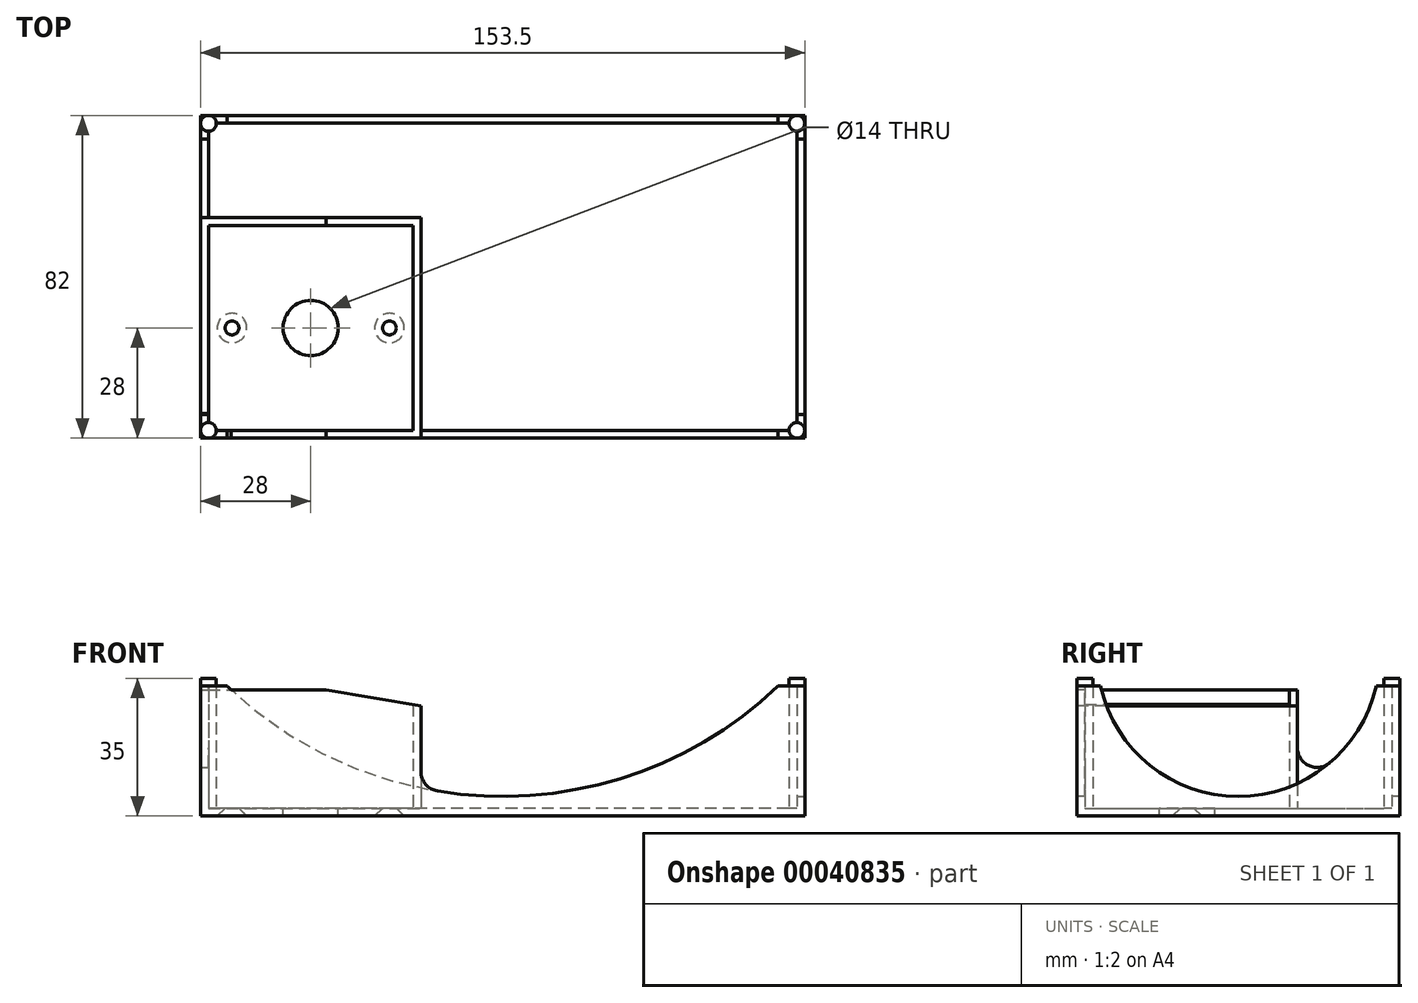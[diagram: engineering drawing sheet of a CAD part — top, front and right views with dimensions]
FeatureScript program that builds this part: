
annotation { "Feature Type Name" : "Feature", "Feature Type Description" : "" }
export const myFeature = defineFeature(function(context is Context, id is Id, definition is map)
    precondition{}
    {
        {
            var Q0;
            Q0=qCreatedBy(makeId("Top.planeOp"),FACE);
            var sketch = newSketch(context, id + "F0", { "sketchPlane" : qUnion([Q0])});
            skLineSegment(sketch, "E0.rect.bottom", {"start": v(76.75, -41) * mm, "end": v(-76.75, -41) * mm});
            skLineSegment(sketch, "E0.rect.top", {"start": v(76.75, 41) * mm, "end": v(-76.75, 41) * mm});
            skLineSegment(sketch, "E0.rect.left", {"start": v(76.75, -41) * mm, "end": v(76.75, 41) * mm});
            skLineSegment(sketch, "E0.rect.right", {"start": v(-76.75, -41) * mm, "end": v(-76.75, 41) * mm});
            skPoint(sketch, "E0.rect.middle", {"position": v(0, 0) * mm});
            skSolve(sketch);
        }
        {
            var Q0;
            Q0 = qSketchRegion(id + "F0", true);
            extrude(context, id + "F1", {"entities" : qUnion([Q0]), "depth" : 2 * mm});
        }
        {
            var Q0;
            Q0=makeQuery(id+"F1.opExtrude","CAP_FACE",FACE,{"disambiguationData":[OSD([sQuery(id+"F0.wireOp",EDGE,"E0.rect.bottom"),sQuery(id+"F0.wireOp",EDGE,"E0.rect.top"),sQuery(id+"F0.wireOp",EDGE,"E0.rect.left"),sQuery(id+"F0.wireOp",EDGE,"E0.rect.right")])],"isStart":false});
            var sketch = newSketch(context, id + "F2", { "sketchPlane" : qUnion([Q0])});
            skLineSegment(sketch, "E1", {"start": v(-76.75, -41) * mm, "end": v(-48.75, -41) * mm, "construction": true});
            skLineSegment(sketch, "E2", {"start": v(-48.75, -41) * mm, "end": v(-48.75, -13) * mm, "construction": true});
            skCircle(sketch, "E3", {"center": v(-48.75, -13) * mm, "radius": 7 * mm});
            skLineSegment(sketch, "E4", {"start": v(-68.75, -13) * mm, "end": v(-28.75, -13) * mm, "construction": true});
            skCircle(sketch, "E5", {"center": v(-68.75, -13) * mm, "radius": 1.75 * mm});
            skCircle(sketch, "E6", {"center": v(-28.75, -13) * mm, "radius": 1.75 * mm});
            skSolve(sketch);
        }
        {
            var Q0;
            Q0 = qSketchRegion(id + "F2", true);
            extrude(context, id + "F3", {"entities" : qUnion([Q0]), "operationType" : NewBodyOperationType.REMOVE, "endBound" : BoundingType.THROUGH_ALL, "oppositeDirection" : true, "depth" : 25 * mm});
        }
        {
            var Q0;
            Q0=makeQuery(id+"F3.boolean.opBoolean","INTERSECT",EDGE,{"derivedFrom":[makeQuery(id+"F1.opExtrude","CAP_FACE",FACE,{"disambiguationData":[OSD([sQuery(id+"F0.wireOp",EDGE,"E0.rect.bottom"),sQuery(id+"F0.wireOp",EDGE,"E0.rect.top"),sQuery(id+"F0.wireOp",EDGE,"E0.rect.left"),sQuery(id+"F0.wireOp",EDGE,"E0.rect.right")])],"isStart":true}),makeQuery(id+"F3.opExtrude","SWEPT_FACE",FACE,{"disambiguationData":[OSD([sQuery(id+"F2.wireOp",EDGE,"E5")])]})]});
            var Q1;
            Q1=makeQuery(id+"F3.boolean.opBoolean","INTERSECT",EDGE,{"derivedFrom":[makeQuery(id+"F1.opExtrude","CAP_FACE",FACE,{"disambiguationData":[OSD([sQuery(id+"F0.wireOp",EDGE,"E0.rect.bottom"),sQuery(id+"F0.wireOp",EDGE,"E0.rect.top"),sQuery(id+"F0.wireOp",EDGE,"E0.rect.left"),sQuery(id+"F0.wireOp",EDGE,"E0.rect.right")])],"isStart":true}),makeQuery(id+"F3.opExtrude","SWEPT_FACE",FACE,{"disambiguationData":[OSD([sQuery(id+"F2.wireOp",EDGE,"E6")])]})]});
            chamfer(context, id + "F4", {"entities" : qUnion([Q0, Q1]), "width" : 2 * mm, "tangentPropagation" : true});
        }
        {
            var Q0;
            {var subQ0=sQuery(id+"F0.wireOp",EDGE,"E0.rect.bottom");var subQ1=sQuery(id+"F0.wireOp",EDGE,"E0.rect.top");var subQ2=sQuery(id+"F0.wireOp",EDGE,"E0.rect.left");var subQ3=sQuery(id+"F0.wireOp",EDGE,"E0.rect.right");Q0=makeQuery(id+"F14.boolean.opBoolean","SPLIT",FACE,{"disambiguationData":[TD([makeQuery(id+"F1.opExtrude","SWEPT_FACE",FACE,{"disambiguationData":[OSD([subQ0])]})])],"derivedFrom":makeQuery(id+"F1.opExtrude","CAP_FACE",FACE,{"disambiguationData":[OSD([subQ0,subQ1,subQ2,subQ3])],"isStart":false})});}
            var sketch = newSketch(context, id + "F5", { "sketchPlane" : qUnion([Q0])});
            skCircle(sketch, "E7", {"center": v(-74.75, 39) * mm, "radius": 2 * mm});
            skLineSegment(sketch, "E8", {"start": v(0, 0) * mm, "end": v(0, 6.22) * mm, "construction": true});
            skLineSegment(sketch, "E9", {"start": v(0, 0) * mm, "end": v(8.64, 0) * mm, "construction": true});
            skCircle(sketch, "E10.MirrorC", {"center": v(74.75, 39) * mm, "radius": 2 * mm});
            skCircle(sketch, "E11.MirrorC", {"center": v(-74.75, -39) * mm, "radius": 2 * mm});
            skCircle(sketch, "E12.MirrorC", {"center": v(74.75, -39) * mm, "radius": 2 * mm});
            skSolve(sketch);
        }
        {
            var Q0;
            Q0 = qSketchRegion(id + "F5", true);
            extrude(context, id + "F6", {"entities" : qUnion([Q0]), "operationType" : NewBodyOperationType.ADD, "depth" : 33 * mm});
        }
        {
            var Q0;
            {var subQ0=sQuery(id+"F0.wireOp",EDGE,"E0.rect.bottom");var subQ1=sQuery(id+"F0.wireOp",EDGE,"E0.rect.top");var subQ2=sQuery(id+"F0.wireOp",EDGE,"E0.rect.left");var subQ3=sQuery(id+"F0.wireOp",EDGE,"E0.rect.right");var subQ4=makeQuery(id+"F1.opExtrude","CAP_FACE",FACE,{"disambiguationData":[OSD([subQ0,subQ1,subQ2,subQ3])],"isStart":false});var subQ5=makeQuery(id+"F14.opExtrude","SWEPT_FACE",FACE,{"disambiguationData":[OSD([sQuery(id+"F13.wireOp",EDGE,"E25.rect.left")])]});var subQ6=makeQuery(id+"F14.opExtrude","SWEPT_FACE",FACE,{"disambiguationData":[OSD([sQuery(id+"F13.wireOp",EDGE,"E25.rect.top")])]});var subQ7=makeQuery(id+"F14.opExtrude","SWEPT_FACE",FACE,{"disambiguationData":[OSD([sQuery(id+"F13.wireOp",EDGE,"E25.rect.right")])]});var subQ8=makeQuery(id+"F14.opExtrude","SWEPT_FACE",FACE,{"disambiguationData":[OSD([sQuery(id+"F13.wireOp",EDGE,"E25.rect.bottom")])]});var subQ9=makeQuery(id+"F1.opExtrude","SWEPT_FACE",FACE,{"disambiguationData":[OSD([subQ0])]});var subQ10=makeQuery(id+"F1.opExtrude","SWEPT_FACE",FACE,{"disambiguationData":[OSD([subQ1])]});var subQ11=makeQuery(id+"F1.opExtrude","SWEPT_FACE",FACE,{"disambiguationData":[OSD([subQ2])]});var subQ12=makeQuery(id+"F1.opExtrude","SWEPT_FACE",FACE,{"disambiguationData":[OSD([subQ3])]});Q0=makeQuery(id+"F6.boolean.opBoolean","SPLIT",FACE,{"disambiguationData":[TD([subQ9,subQ4,subQ10,subQ11,subQ12,subQ8,subQ6,subQ5,subQ7,makeQuery(id+"F6.opExtrude","SWEPT_FACE",FACE,{"disambiguationData":[OSD([sQuery(id+"F5.wireOp",EDGE,"E7")])]}),makeQuery(id+"F6.opExtrude","SWEPT_FACE",FACE,{"disambiguationData":[OSD([sQuery(id+"F5.wireOp",EDGE,"E10.MirrorC")])]}),makeQuery(id+"F6.opExtrude","SWEPT_FACE",FACE,{"disambiguationData":[OSD([sQuery(id+"F5.wireOp",EDGE,"E12.MirrorC")])]})])],"derivedFrom":makeQuery(id+"F14.boolean.opBoolean","SPLIT",FACE,{"disambiguationData":[TD([subQ9])],"derivedFrom":subQ4})});}
            var sketch = newSketch(context, id + "F7", { "sketchPlane" : qUnion([Q0])});
            skLineSegment(sketch, "E13.rect.bottom", {"start": v(76.75, -41) * mm, "end": v(-76.75, -41) * mm});
            skLineSegment(sketch, "E13.rect.top", {"start": v(76.75, 41) * mm, "end": v(-76.75, 41) * mm});
            skLineSegment(sketch, "E13.rect.left", {"start": v(76.75, -41) * mm, "end": v(76.75, 41) * mm});
            skLineSegment(sketch, "E13.rect.right", {"start": v(-76.75, -41) * mm, "end": v(-76.75, 41) * mm});
            skPoint(sketch, "E13.rect.middle", {"position": v(0, 0) * mm});
            skLineSegment(sketch, "E14.rect.bottom", {"start": v(74.75, -39) * mm, "end": v(-74.75, -39) * mm});
            skLineSegment(sketch, "E14.rect.top", {"start": v(74.75, 39) * mm, "end": v(-74.75, 39) * mm});
            skLineSegment(sketch, "E14.rect.left", {"start": v(74.75, -39) * mm, "end": v(74.75, 39) * mm});
            skLineSegment(sketch, "E14.rect.right", {"start": v(-74.75, -39) * mm, "end": v(-74.75, 39) * mm});
            skLineSegment(sketch, "E15", {"start": v(74.75, 0) * mm, "end": v(76.75, 0) * mm, "construction": true});
            skLineSegment(sketch, "E16", {"start": v(0, -39) * mm, "end": v(0, -41) * mm, "construction": true});
            skSolve(sketch);
        }
        {
            var Q0;
            Q0 = qSketchRegion(id + "F7", true);
            extrude(context, id + "F8", {"entities" : qUnion([Q0]), "operationType" : NewBodyOperationType.ADD, "depth" : 31 * mm});
        }
        {
            var Q0;
            Q0=makeQuery(id+"F8.boolean.opBoolean","MERGE",FACE,{"derivedFrom":[makeQuery(id+"F14.boolean.opBoolean","MERGE",FACE,{"derivedFrom":[makeQuery(id+"F1.opExtrude","SWEPT_FACE",FACE,{"disambiguationData":[OSD([sQuery(id+"F0.wireOp",EDGE,"E0.rect.bottom")])]}),makeQuery(id+"F14.opExtrude","SWEPT_FACE",FACE,{"disambiguationData":[OSD([sQuery(id+"F13.wireOp",EDGE,"E25.rect.bottom")])]})]}),makeQuery(id+"F8.opExtrude","SWEPT_FACE",FACE,{"disambiguationData":[OSD([sQuery(id+"F7.wireOp",EDGE,"E13.rect.bottom")])]})]});
            var sketch = newSketch(context, id + "F9", { "sketchPlane" : qUnion([Q0])});
            skLineSegment(sketch, "E17", {"start": v(0, 0) * mm, "end": v(0, 5) * mm, "construction": true});
            skPoint(sketch, "E17.endSnap0", {"position": v(0, 0) * mm});
            skLineSegment(sketch, "E18", {"start": v(-70, 33) * mm, "end": v(70, 33) * mm});
            skPoint(sketch, "E19", {"position": v(0, 33) * mm});
            skArc(sketch, "E20", {"start": v(-70, 33) * mm, "mid": v(0, 5) * mm, "end": v(70, 33) * mm});
            skSolve(sketch);
        }
        {
            var Q0;
            Q0 = qSketchRegion(id + "F9", true);
            extrude(context, id + "F10", {"entities" : qUnion([Q0]), "operationType" : NewBodyOperationType.REMOVE, "endBound" : BoundingType.THROUGH_ALL, "oppositeDirection" : true, "depth" : 25 * mm});
        }
        {
            var Q0;
            Q0=makeQuery(id+"F8.boolean.opBoolean","MERGE",FACE,{"derivedFrom":[makeQuery(id+"F1.opExtrude","SWEPT_FACE",FACE,{"disambiguationData":[OSD([sQuery(id+"F0.wireOp",EDGE,"E0.rect.left")])]}),makeQuery(id+"F8.opExtrude","SWEPT_FACE",FACE,{"disambiguationData":[OSD([sQuery(id+"F7.wireOp",EDGE,"E13.rect.left")])]})]});
            var sketch = newSketch(context, id + "F11", { "sketchPlane" : qUnion([Q0])});
            skLineSegment(sketch, "E21", {"start": v(-35, 33) * mm, "end": v(35, 33) * mm});
            skPoint(sketch, "E22", {"position": v(0, 33) * mm});
            skLineSegment(sketch, "E23", {"start": v(0, 0) * mm, "end": v(0, 5) * mm, "construction": true});
            skPoint(sketch, "E23.endSnap0", {"position": v(0, 0) * mm});
            skArc(sketch, "E24", {"start": v(-35, 33) * mm, "mid": v(0, 5) * mm, "end": v(35, 33) * mm});
            skSolve(sketch);
        }
        {
            var Q0;
            Q0 = qSketchRegion(id + "F11", true);
            extrude(context, id + "F12", {"entities" : qUnion([Q0]), "operationType" : NewBodyOperationType.REMOVE, "endBound" : BoundingType.THROUGH_ALL, "oppositeDirection" : true, "depth" : 25 * mm});
        }
        {
            var Q0;
            Q0=makeQuery(id+"F1.opExtrude","CAP_FACE",FACE,{"disambiguationData":[OSD([sQuery(id+"F0.wireOp",EDGE,"E0.rect.bottom"),sQuery(id+"F0.wireOp",EDGE,"E0.rect.top"),sQuery(id+"F0.wireOp",EDGE,"E0.rect.left"),sQuery(id+"F0.wireOp",EDGE,"E0.rect.right")])],"isStart":false});
            var sketch = newSketch(context, id + "F13", { "sketchPlane" : qUnion([Q0])});
            skLineSegment(sketch, "E25.rect.bottom", {"start": v(-76.75, -41) * mm, "end": v(-20.75, -41) * mm});
            skLineSegment(sketch, "E25.rect.top", {"start": v(-76.75, 15) * mm, "end": v(-20.75, 15) * mm});
            skLineSegment(sketch, "E25.rect.left", {"start": v(-76.75, -41) * mm, "end": v(-76.75, 15) * mm});
            skLineSegment(sketch, "E25.rect.right", {"start": v(-20.75, -41) * mm, "end": v(-20.75, 15) * mm});
            skPoint(sketch, "E25.rect.middle", {"position": v(-48.75, -13) * mm});
            skLineSegment(sketch, "E26.0", {"start": v(-74.75, 13) * mm, "end": v(-22.75, 13) * mm});
            skLineSegment(sketch, "E26.1", {"start": v(-74.75, -39) * mm, "end": v(-74.75, 13) * mm});
            skLineSegment(sketch, "E26.2", {"start": v(-74.75, -39) * mm, "end": v(-22.75, -39) * mm});
            skLineSegment(sketch, "E26.3", {"start": v(-22.75, -39) * mm, "end": v(-22.75, 13) * mm});
            skLineSegment(sketch, "E27", {"start": v(-48.75, -13) * mm, "end": v(-16.75, -13) * mm, "construction": true});
            skCircle(sketch, "E28", {"center": v(-16.75, -13) * mm, "radius": 2 * mm, "construction": true});
            skSolve(sketch);
        }
        {
            var Q0;
            Q0 = qSketchRegion(id + "F13", true);
            extrude(context, id + "F14", {"entities" : qUnion([Q0]), "operationType" : NewBodyOperationType.ADD, "depth" : 30 * mm});
        }
        {
            var Q0;
            Q0=makeQuery(id+"F14.boolean.opBoolean","MERGE",FACE,{"derivedFrom":[makeQuery(id+"F8.boolean.opBoolean","MERGE",FACE,{"derivedFrom":[makeQuery(id+"F1.opExtrude","SWEPT_FACE",FACE,{"disambiguationData":[OSD([sQuery(id+"F0.wireOp",EDGE,"E0.rect.bottom")])]}),makeQuery(id+"F8.opExtrude","SWEPT_FACE",FACE,{"disambiguationData":[OSD([sQuery(id+"F7.wireOp",EDGE,"E13.rect.bottom")])]})]}),makeQuery(id+"F14.opExtrude","SWEPT_FACE",FACE,{"disambiguationData":[OSD([sQuery(id+"F13.wireOp",EDGE,"E25.rect.bottom")])]})]});
            var sketch = newSketch(context, id + "F15", { "sketchPlane" : qUnion([Q0])});
            skLineSegment(sketch, "E29", {"start": v(-20.75, 32) * mm, "end": v(-20.75, 28) * mm});
            skLineSegment(sketch, "E30", {"start": v(-20.75, 28) * mm, "end": v(-44.84, 32) * mm});
            skLineSegment(sketch, "E31", {"start": v(-44.84, 32) * mm, "end": v(-20.75, 32) * mm});
            skSolve(sketch);
        }
        {
            var Q0;
            Q0 = qSketchRegion(id + "F15", true);
            extrude(context, id + "F16", {"entities" : qUnion([Q0]), "operationType" : NewBodyOperationType.REMOVE, "endBound" : BoundingType.THROUGH_ALL, "oppositeDirection" : true, "depth" : 25 * mm});
        }
        {
            var Q0;
            Q0=makeQuery(id+"F14.boolean.opBoolean","INTERSECT",EDGE,{"derivedFrom":[makeQuery(id+"F12.boolean.opBoolean","COPY",FACE,{"disambiguationData":[OD(1.0)],"derivedFrom":makeQuery(id+"F12.opExtrude","SWEPT_FACE",FACE,{"disambiguationData":[OSD([sQuery(id+"F11.wireOp",EDGE,"E24")])]})}),makeQuery(id+"F14.opExtrude","SWEPT_FACE",FACE,{"disambiguationData":[OSD([sQuery(id+"F13.wireOp",EDGE,"E25.rect.top")])]})]});
            var Q1;
            Q1=makeQuery(id+"F14.boolean.opBoolean","INTERSECT",EDGE,{"derivedFrom":[makeQuery(id+"F10.boolean.opBoolean","COPY",FACE,{"disambiguationData":[OD(0.0)],"derivedFrom":makeQuery(id+"F10.opExtrude","SWEPT_FACE",FACE,{"disambiguationData":[OSD([sQuery(id+"F9.wireOp",EDGE,"E20")])]})}),makeQuery(id+"F14.opExtrude","SWEPT_FACE",FACE,{"disambiguationData":[OSD([sQuery(id+"F13.wireOp",EDGE,"E25.rect.right")])]})]});
            fillet(context, id + "F17", {"entities" : qUnion([Q0, Q1]), "radius" : 5 * mm, "tangentPropagation" : true, "allowEdgeOverflow" : false});
        }
    });
